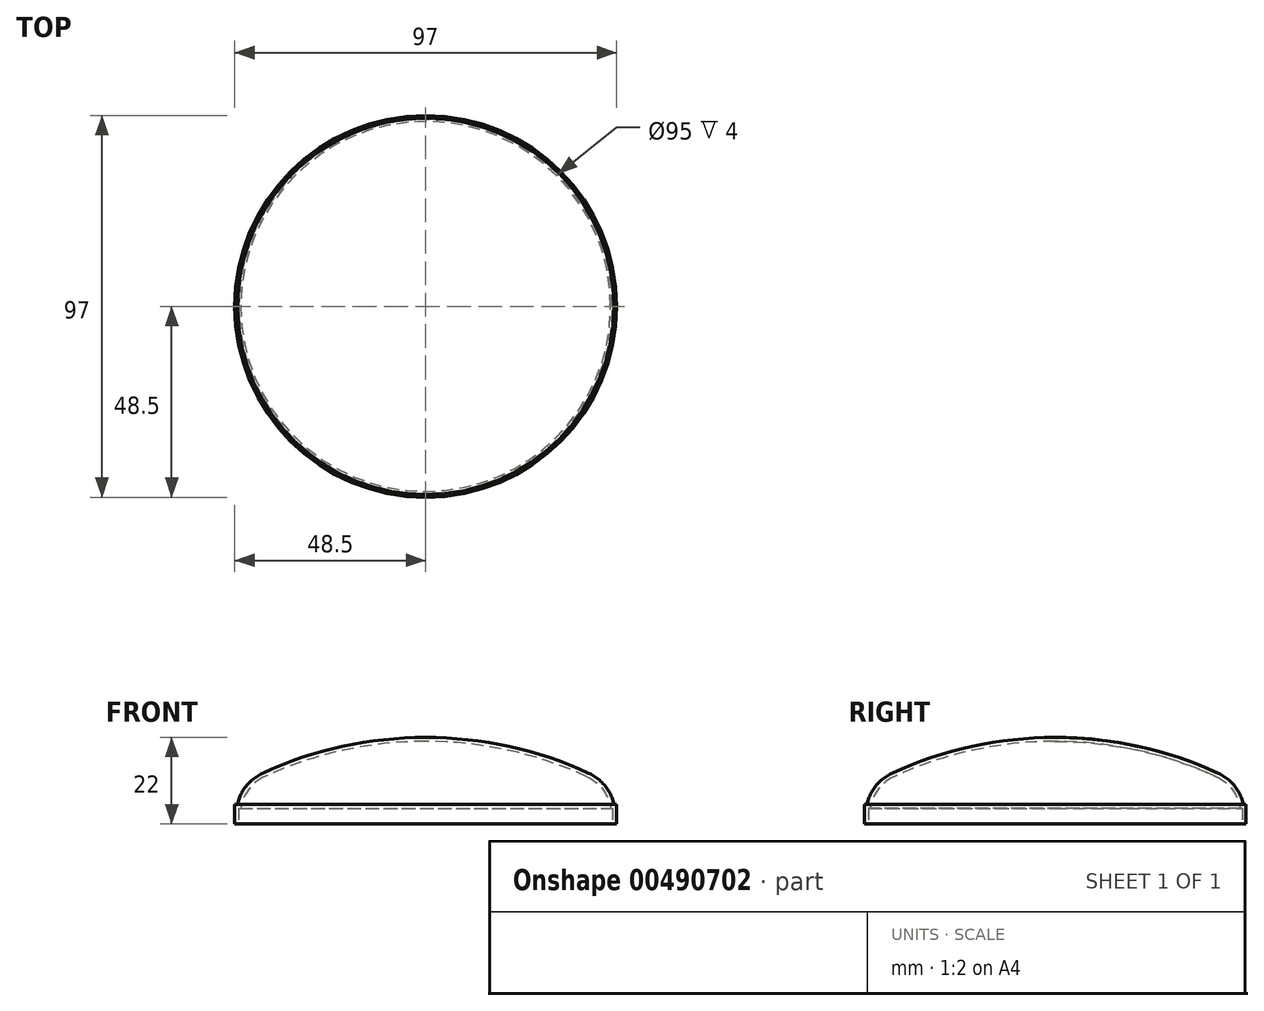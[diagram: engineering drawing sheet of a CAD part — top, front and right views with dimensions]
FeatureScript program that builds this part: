
annotation { "Feature Type Name" : "Feature", "Feature Type Description" : "" }
export const myFeature = defineFeature(function(context is Context, id is Id, definition is map)
    precondition{}
    {
        {
            var Q0;
            Q0=qCreatedBy(makeId("Right.planeOp"),FACE);
            var sketch = newSketch(context, id + "F0", { "sketchPlane" : qUnion([Q0])});
            skLineSegment(sketch, "E0", {"start": v(0, 0) * mm, "end": v(41, 0) * mm, "construction": true});
            skLineSegment(sketch, "E1", {"start": v(0, 0) * mm, "end": v(0, 9) * mm, "construction": true});
            skLineSegment(sketch, "E2", {"start": v(0, 0) * mm, "end": v(0, -8) * mm, "construction": true});
            skLineSegment(sketch, "E3", {"start": v(0, -8) * mm, "end": v(47, -8) * mm, "construction": true});
            skLineSegment(sketch, "E4", {"start": v(0, 0) * mm, "end": v(-41, 0) * mm, "construction": true});
            skArc(sketch, "E5", {"start": v(41, 0) * mm, "mid": v(20.99, 6.72) * mm, "end": v(0, 9) * mm});
            skArc(sketch, "E6", {"start": v(41, 0) * mm, "mid": v(45.01, -3.24) * mm, "end": v(47, -8) * mm});
            skPoint(sketch, "E7.endSnap0", {"position": v(0, 4.5) * mm});
            skPoint(sketch, "E8.orphan", {"position": v(0, 13.16) * mm});
            skLineSegment(sketch, "E9.0", {"start": v(0, -12) * mm, "end": v(47.5, -12) * mm, "construction": true});
            skLineSegment(sketch, "E10.0", {"start": v(47.5, -8) * mm, "end": v(47.5, -12) * mm});
            skLineSegment(sketch, "E11", {"start": v(47, -8) * mm, "end": v(47.5, -8) * mm});
            skArc(sketch, "E12.0", {"start": v(41.42, 0.9) * mm, "mid": v(21.2, 7.7) * mm, "end": v(0, 10) * mm});
            skArc(sketch, "E12.1", {"start": v(41.42, 0.9) * mm, "mid": v(45.54, -2.3) * mm, "end": v(47.83, -7) * mm});
            skLineSegment(sketch, "E12.2", {"start": v(47.83, -7) * mm, "end": v(48.5, -7) * mm});
            skLineSegment(sketch, "E12.3", {"start": v(48.5, -7) * mm, "end": v(48.5, -12) * mm});
            skLineSegment(sketch, "E13", {"start": v(0, 10) * mm, "end": v(0, 9) * mm});
            skLineSegment(sketch, "E14", {"start": v(47.5, -12) * mm, "end": v(48.5, -12) * mm});
            skSolve(sketch);
        }
        {
            var Q0;
            Q0=makeQuery(id+"F0.imprint","IMPRINT",FACE,{"disambiguationData":[TD([[makeQuery(id+"F0.imprint","IMPRINT",EDGE,{"derivedFrom":sQuery(id+"F0.wireOp",EDGE,"E5")}),-1.0]])]});
            var Q1;
            Q1=sQuery(id+"F0.wireOp",EDGE,"E1");
            revolve(context, id + "F1", {"entities" : qUnion([Q0]), "axis" : qUnion([Q1]), "revolveType" : RevolveType.FULL});
        }
    });
